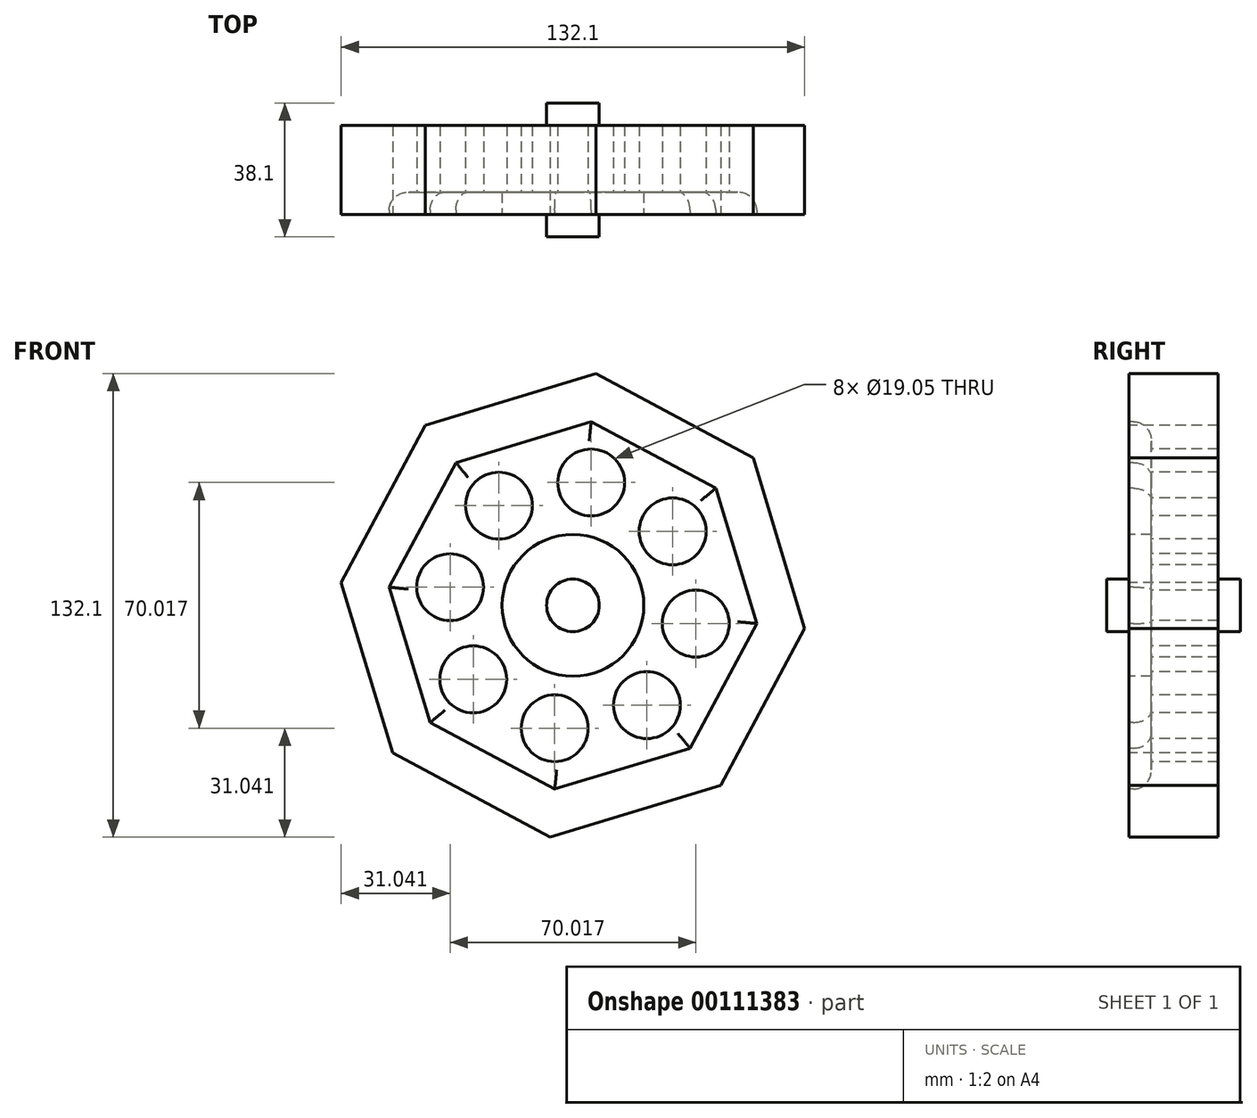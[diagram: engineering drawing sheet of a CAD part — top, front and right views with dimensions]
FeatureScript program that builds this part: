
annotation { "Feature Type Name" : "Feature", "Feature Type Description" : "" }
export const myFeature = defineFeature(function(context is Context, id is Id, definition is map)
    precondition{}
    {
        {
            var Q0;
            Q0=qCreatedBy(makeId("Front.planeOp"),FACE);
            var sketch = newSketch(context, id + "F0", { "sketchPlane" : qUnion([Q0])});
            skCircle(sketch, "E0.cCircle", {"center": v(0, 0) * mm, "radius": 61.32 * mm, "construction": true});
            skLineSegment(sketch, "E0.0", {"start": v(51.33, 42.08) * mm, "end": v(66.05, -6.55) * mm});
            skLineSegment(sketch, "E0.1", {"start": v(66.05, -6.55) * mm, "end": v(42.08, -51.33) * mm});
            skLineSegment(sketch, "E0.2", {"start": v(42.08, -51.33) * mm, "end": v(-6.55, -66.05) * mm});
            skLineSegment(sketch, "E0.3", {"start": v(-6.55, -66.05) * mm, "end": v(-51.33, -42.08) * mm});
            skLineSegment(sketch, "E0.4", {"start": v(-51.33, -42.08) * mm, "end": v(-66.05, 6.55) * mm});
            skLineSegment(sketch, "E0.5", {"start": v(-66.05, 6.55) * mm, "end": v(-42.08, 51.33) * mm});
            skLineSegment(sketch, "E0.6", {"start": v(-42.08, 51.33) * mm, "end": v(6.55, 66.05) * mm});
            skLineSegment(sketch, "E0.7", {"start": v(6.55, 66.05) * mm, "end": v(51.33, 42.08) * mm});
            skPoint(sketch, "E0.0.midPoint", {"position": v(58.7, 17.76) * mm});
            skCircle(sketch, "E1", {"center": v(0, 0) * mm, "radius": 7.5 * mm});
            skSolve(sketch);
        }
        {
            var Q0;
            Q0=makeQuery(id+"F0.imprint","IMPRINT",FACE,{"disambiguationData":[TD([[makeQuery(id+"F0.imprint","IMPRINT",EDGE,{"derivedFrom":sQuery(id+"F0.wireOp",EDGE,"E0.0")}),-1.0]])]});
            extrude(context, id + "F1", {"entities" : qUnion([Q0]), "endBound" : BoundingType.SYMMETRIC, "oppositeDirection" : true, "depth" : 25.4 * mm});
        }
        {
            var Q0;
            Q0=makeQuery(id+"F0.imprint","IMPRINT",FACE,{"disambiguationData":[TD([[makeQuery(id+"F0.imprint","IMPRINT",EDGE,{"derivedFrom":sQuery(id+"F0.wireOp",EDGE,"E1")}),1.0]])]});
            extrude(context, id + "F2", {"entities" : qUnion([Q0]), "operationType" : NewBodyOperationType.ADD, "endBound" : BoundingType.SYMMETRIC, "depth" : 38.1 * mm});
        }
        {
            var Q0;
            Q0=makeQuery(id+"F1.opExtrude","CAP_FACE",FACE,{"disambiguationData":[OSD([sQuery(id+"F0.wireOp",EDGE,"E0.0"),sQuery(id+"F0.wireOp",EDGE,"E0.1"),sQuery(id+"F0.wireOp",EDGE,"E0.2"),sQuery(id+"F0.wireOp",EDGE,"E0.3"),sQuery(id+"F0.wireOp",EDGE,"E0.4"),sQuery(id+"F0.wireOp",EDGE,"E0.5"),sQuery(id+"F0.wireOp",EDGE,"E0.6"),sQuery(id+"F0.wireOp",EDGE,"E0.7"),sQuery(id+"F0.wireOp",EDGE,"E1")])],"isStart":true});
            var sketch = newSketch(context, id + "F3", { "sketchPlane" : qUnion([Q0])});
            skLineSegment(sketch, "E2.0", {"start": v(-42.08, 51.33) * mm, "end": v(6.55, 66.05) * mm});
            skLineSegment(sketch, "E3.0", {"start": v(6.55, 66.05) * mm, "end": v(51.33, 42.08) * mm});
            skLineSegment(sketch, "E4.0", {"start": v(51.33, 42.08) * mm, "end": v(66.05, -6.55) * mm});
            skLineSegment(sketch, "E5.0", {"start": v(66.05, -6.55) * mm, "end": v(42.08, -51.33) * mm});
            skLineSegment(sketch, "E6.0", {"start": v(42.08, -51.33) * mm, "end": v(-6.55, -66.05) * mm});
            skLineSegment(sketch, "E7.0", {"start": v(-6.55, -66.05) * mm, "end": v(-51.33, -42.08) * mm});
            skLineSegment(sketch, "E8.0", {"start": v(-51.33, -42.08) * mm, "end": v(-66.05, 6.55) * mm});
            skLineSegment(sketch, "E9.0", {"start": v(-66.05, 6.55) * mm, "end": v(-42.08, 51.33) * mm});
            skLineSegment(sketch, "E10.0", {"start": v(33.36, -40.7) * mm, "end": v(52.37, -5.2) * mm});
            skLineSegment(sketch, "E10.1", {"start": v(-5.2, -52.37) * mm, "end": v(33.36, -40.7) * mm});
            skLineSegment(sketch, "E10.2", {"start": v(52.37, -5.2) * mm, "end": v(40.7, 33.36) * mm});
            skLineSegment(sketch, "E10.3", {"start": v(-40.7, -33.36) * mm, "end": v(-5.2, -52.37) * mm});
            skLineSegment(sketch, "E10.4", {"start": v(40.7, 33.36) * mm, "end": v(5.2, 52.37) * mm});
            skLineSegment(sketch, "E10.5", {"start": v(5.2, 52.37) * mm, "end": v(-33.36, 40.7) * mm});
            skLineSegment(sketch, "E10.6", {"start": v(-33.36, 40.7) * mm, "end": v(-52.37, 5.2) * mm});
            skLineSegment(sketch, "E10.7", {"start": v(-52.37, 5.2) * mm, "end": v(-40.7, -33.36) * mm});
            skCircle(sketch, "E11.0", {"center": v(0, 0) * mm, "radius": 20.2 * mm});
            skCircle(sketch, "E12", {"center": v(5.2, 35) * mm, "radius": 9.53 * mm});
            skCircle(sketch, "E13.1.0", {"center": v(-21.08, 28.43) * mm, "radius": 9.53 * mm});
            skCircle(sketch, "E13.2.0", {"center": v(-35, 5.2) * mm, "radius": 9.53 * mm});
            skCircle(sketch, "E13.3.0", {"center": v(-28.43, -21.08) * mm, "radius": 9.53 * mm});
            skCircle(sketch, "E13.4.0", {"center": v(-5.2, -35) * mm, "radius": 9.53 * mm});
            skCircle(sketch, "E13.5.0", {"center": v(21.08, -28.43) * mm, "radius": 9.53 * mm});
            skCircle(sketch, "E13.6.0", {"center": v(35, -5.2) * mm, "radius": 9.53 * mm});
            skCircle(sketch, "E13.7.0", {"center": v(28.43, 21.08) * mm, "radius": 9.53 * mm});
            skSolve(sketch);
        }
        {
            var Q0;
            Q0=makeQuery(id+"F3.imprint","IMPRINT",FACE,{"disambiguationData":[TD([[makeQuery(id+"F3.imprint","IMPRINT",EDGE,{"derivedFrom":sQuery(id+"F3.wireOp",EDGE,"E10.0")}),1.0]])]});
            extrude(context, id + "F4", {"entities" : qUnion([Q0]), "operationType" : NewBodyOperationType.REMOVE, "oppositeDirection" : true, "depth" : 6.35 * mm});
        }
        {
            var Q0;
            Q0=makeQuery(id+"F3.imprint","IMPRINT",FACE,{"disambiguationData":[TD([[makeQuery(id+"F3.imprint","IMPRINT",EDGE,{"derivedFrom":sQuery(id+"F3.wireOp",EDGE,"E13.2.0")}),1.0]])]});
            var Q1;
            Q1=makeQuery(id+"F3.imprint","IMPRINT",FACE,{"disambiguationData":[TD([[makeQuery(id+"F3.imprint","IMPRINT",EDGE,{"derivedFrom":sQuery(id+"F3.wireOp",EDGE,"E13.1.0")}),1.0]])]});
            var Q2;
            Q2=makeQuery(id+"F3.imprint","IMPRINT",FACE,{"disambiguationData":[TD([[makeQuery(id+"F3.imprint","IMPRINT",EDGE,{"derivedFrom":sQuery(id+"F3.wireOp",EDGE,"E12")}),1.0]])]});
            var Q3;
            Q3=makeQuery(id+"F3.imprint","IMPRINT",FACE,{"disambiguationData":[TD([[makeQuery(id+"F3.imprint","IMPRINT",EDGE,{"derivedFrom":sQuery(id+"F3.wireOp",EDGE,"E13.7.0")}),1.0]])]});
            var Q4;
            Q4=makeQuery(id+"F3.imprint","IMPRINT",FACE,{"disambiguationData":[TD([[makeQuery(id+"F3.imprint","IMPRINT",EDGE,{"derivedFrom":sQuery(id+"F3.wireOp",EDGE,"E13.5.0")}),1.0]])]});
            var Q5;
            Q5=makeQuery(id+"F3.imprint","IMPRINT",FACE,{"disambiguationData":[TD([[makeQuery(id+"F3.imprint","IMPRINT",EDGE,{"derivedFrom":sQuery(id+"F3.wireOp",EDGE,"E13.3.0")}),1.0]])]});
            var Q6;
            Q6=makeQuery(id+"F3.imprint","IMPRINT",FACE,{"disambiguationData":[TD([[makeQuery(id+"F3.imprint","IMPRINT",EDGE,{"derivedFrom":sQuery(id+"F3.wireOp",EDGE,"E13.6.0")}),1.0]])]});
            var Q7;
            Q7=makeQuery(id+"F3.imprint","IMPRINT",FACE,{"disambiguationData":[TD([[makeQuery(id+"F3.imprint","IMPRINT",EDGE,{"derivedFrom":sQuery(id+"F3.wireOp",EDGE,"E13.4.0")}),1.0]])]});
            extrude(context, id + "F5", {"entities" : qUnion([Q0, Q1, Q2, Q3, Q4, Q5, Q6, Q7]), "operationType" : NewBodyOperationType.REMOVE, "endBound" : BoundingType.THROUGH_ALL, "oppositeDirection" : true, "depth" : 25.4 * mm});
        }
        {
            var Q0;
            Q0=makeQuery(id+"F4.boolean.opBoolean","COPY",EDGE,{"derivedFrom":makeQuery(id+"F4.opExtrude","CAP_EDGE",EDGE,{"disambiguationData":[OSD([sQuery(id+"F3.wireOp",EDGE,"E10.5")])],"isStart":false})});
            var Q1;
            Q1=makeQuery(id+"F4.boolean.opBoolean","COPY",EDGE,{"derivedFrom":makeQuery(id+"F4.opExtrude","CAP_EDGE",EDGE,{"disambiguationData":[OSD([sQuery(id+"F3.wireOp",EDGE,"E10.6")])],"isStart":false})});
            var Q2;
            Q2=makeQuery(id+"F4.boolean.opBoolean","COPY",EDGE,{"derivedFrom":makeQuery(id+"F4.opExtrude","CAP_EDGE",EDGE,{"disambiguationData":[OSD([sQuery(id+"F3.wireOp",EDGE,"E10.7")])],"isStart":false})});
            var Q3;
            Q3=makeQuery(id+"F4.boolean.opBoolean","COPY",EDGE,{"derivedFrom":makeQuery(id+"F4.opExtrude","CAP_EDGE",EDGE,{"disambiguationData":[OSD([sQuery(id+"F3.wireOp",EDGE,"E10.3")])],"isStart":false})});
            var Q4;
            Q4=makeQuery(id+"F4.boolean.opBoolean","COPY",EDGE,{"derivedFrom":makeQuery(id+"F4.opExtrude","CAP_EDGE",EDGE,{"disambiguationData":[OSD([sQuery(id+"F3.wireOp",EDGE,"E10.4")])],"isStart":false})});
            var Q5;
            Q5=makeQuery(id+"F4.boolean.opBoolean","COPY",EDGE,{"derivedFrom":makeQuery(id+"F4.opExtrude","CAP_EDGE",EDGE,{"disambiguationData":[OSD([sQuery(id+"F3.wireOp",EDGE,"E10.2")])],"isStart":false})});
            var Q6;
            Q6=makeQuery(id+"F4.boolean.opBoolean","COPY",EDGE,{"derivedFrom":makeQuery(id+"F4.opExtrude","CAP_EDGE",EDGE,{"disambiguationData":[OSD([sQuery(id+"F3.wireOp",EDGE,"E10.0")])],"isStart":false})});
            var Q7;
            Q7=makeQuery(id+"F4.boolean.opBoolean","COPY",EDGE,{"derivedFrom":makeQuery(id+"F4.opExtrude","CAP_EDGE",EDGE,{"disambiguationData":[OSD([sQuery(id+"F3.wireOp",EDGE,"E10.1")])],"isStart":false})});
            fillet(context, id + "F6", {"entities" : qUnion([Q0, Q1, Q2, Q3, Q4, Q5, Q6, Q7]), "radius" : 5.08 * mm, "tangentPropagation" : true, "allowEdgeOverflow" : false});
        }
    });
